# Revit family: STRIPE BLOCK RAIL 964_DTM40U.9.2.90
name_source: partatom
category: Luminarias
units: mm (PartAtom-declared; Revit-internal decimal feet)

## family parameters
Compartido = No
Corte con vacíos al cargar = No
Cota de conector redondo = Diámetro de uso
Origen de luz = Sí
Punto de cálculo de habitación = No
Se basa en plano de trabajo = Sí
Siempre vertical = Sí
Tipo de pieza = Normal

## types (3) — shared parameters
Cambio de temperatura de color de luz atenuada = <Ninguno>
Comentarios de vataje = 90-240V
Elevación por defecto = 1219 mm
Fabricante = BRILLANT
Filtro de color = 16777215
Longitud de símbolo de origen de luz = 3048 mm  [stored 10 ft]
Lámpara = 2835SMD SAMSUNG
Watt per fixture = 40
Ángulo de campo de foco = 90.00°
Ángulo de enfoque = 90.00°
Ángulo de inclinación = 60.00°

## per-type parameters (varying)
| type | Descripción | Modelo |
| STRIPE BLOCK RAIL 964_DTM40U.9.2.90 | LUMINARIA DOWNLIGHT EN FORMATO RECTANGULAR COMPATIBLE CON RIEL DE 6 ENTRADAS Y 3 CIRCUITOS, CUERPO DE ALUMINIO ACABADO EN COLOR NEGRO, IP 20, PESO 1.88Kg, TIPO DE LED 2835SMD SAMSUNG CON 40W TOTAL, 3050 LUMENES, 79LM/W, IRC 90, TEMPERATURA EN BLANCO CALIDO 2700K, 50 MIL HORAS DE VIDA PROMEDIO, APERTURA DE 90 GRADOS POR STOCK, ALIMENTADO A 90-240V | DTM40U.9.2.90 |
| STRIPE BLOCK RAIL 964_DTM40W.9.2.90 | LUMINARIA DOWNLIGHT EN FORMATO RECTANGULAR COMPATIBLE CON RIEL DE 6 ENTRADAS Y 3 CIRCUITOS, CUERPO DE ALUMINIO ACABADO EN COLOR NEGRO, IP 20, PESO 1.88Kg, TIPO DE LED 2835SMD SAMSUNG CON 40W TOTAL, 3100 LUMENES, 80LM/W, IRC 90, TEMPERATURA EN BLANCO CALIDO 3000K, 50 MIL HORAS DE VIDA PROMEDIO, APERTURA DE 90 GRADOS POR STOCK, ALIMENTADO A 90-240V | DTM40W.9.2.90 |
| STRIPE BLOCK RAIL 964_DTM40N.9.2.90 | LUMINARIA DOWNLIGHT EN FORMATO RECTANGULAR COMPATIBLE CON RIEL DE 6 ENTRADAS Y 3 CIRCUITOS, CUERPO DE ALUMINIO ACABADO EN COLOR NEGRO, IP 20, PESO 1.88Kg, TIPO DE LED 2835SMD SAMSUNG CON 40W TOTAL, 3150 LUMENES, 81LM/W, IRC 90, TEMPERATURA EN BLANCO FRIO 4000K, 50 MIL HORAS DE VIDA PROMEDIO, APERTURA DE 90 GRADOS POR STOCK, ALIMENTADO A 90-240V | DTM40N.9.2.90 |

note: [stored X ft] marks values corroborated as IEEE doubles in the binary element streams (Revit-internal decimal feet)

## geometry (parser evidence)
native form markers: Blend x2
no freeform markers — native parametric forms only
